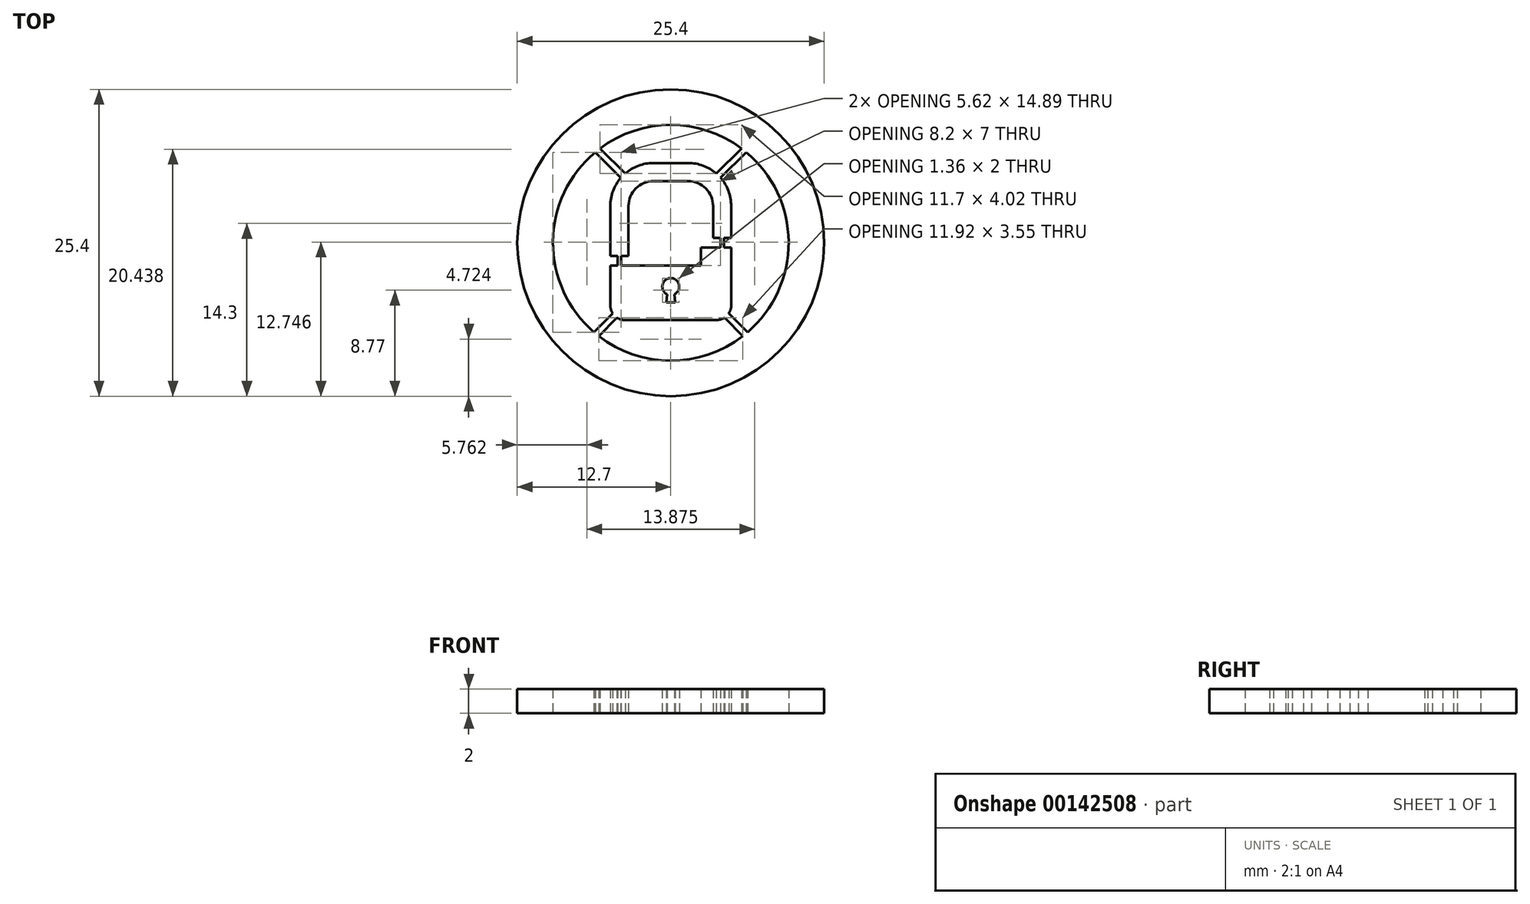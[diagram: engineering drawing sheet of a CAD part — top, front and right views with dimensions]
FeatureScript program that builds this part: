
annotation { "Feature Type Name" : "Feature", "Feature Type Description" : "" }
export const myFeature = defineFeature(function(context is Context, id is Id, definition is map)
    precondition{}
    {
        {
            assignVariable(context, id + "F0", {"name" : "thick", "anyValue" : 2});
        }
        {
            var Q0;
            Q0=qCreatedBy(makeId("Top.planeOp"),FACE);
            var sketch = newSketch(context, id + "F1", { "sketchPlane" : qUnion([Q0])});
            skCircle(sketch, "E0", {"center": v(0, 0) * mm, "radius": 9.75 * mm});
            skCircle(sketch, "E1", {"center": v(0, 0) * mm, "radius": 12.7 * mm});
            skSolve(sketch);
        }
        {
            var Q0;
            Q0=qCreatedBy(makeId("Top.planeOp"),FACE);
            var sketch = newSketch(context, id + "F2", { "sketchPlane" : qUnion([Q0])});
            skLineSegment(sketch, "E2", {"start": v(-3.78, -6.4) * mm, "end": v(3.78, -6.4) * mm});
            skLineSegment(sketch, "E3", {"start": v(5, -5.18) * mm, "end": v(5, -0.4) * mm});
            skLineSegment(sketch, "E4", {"start": v(-5, -5.18) * mm, "end": v(-5, -1.9) * mm});
            skLineSegment(sketch, "E5", {"start": v(-5, -1.9) * mm, "end": v(2.5, -1.9) * mm});
            skLineSegment(sketch, "E6", {"start": v(2.5, -1.9) * mm, "end": v(2.5, -0.4) * mm});
            skLineSegment(sketch, "E7", {"start": v(2.5, -0.4) * mm, "end": v(5, -0.4) * mm});
            skArc(sketch, "E8", {"start": v(3.78, -6.4) * mm, "mid": v(4.64, -6.04) * mm, "end": v(5, -5.18) * mm});
            skArc(sketch, "E9", {"start": v(-3.78, -6.4) * mm, "mid": v(-4.64, -6.04) * mm, "end": v(-5, -5.18) * mm});
            skLineSegment(sketch, "E10", {"start": v(-5, -1.1) * mm, "end": v(-3.5, -1.1) * mm});
            skLineSegment(sketch, "E11", {"start": v(-3.5, -1.1) * mm, "end": v(-3.5, 3.03) * mm});
            skLineSegment(sketch, "E12", {"start": v(-5, -1.1) * mm, "end": v(-5, 3.03) * mm});
            skLineSegment(sketch, "E13", {"start": v(3.5, 0.4) * mm, "end": v(5, 0.4) * mm});
            skLineSegment(sketch, "E14", {"start": v(5, 0.4) * mm, "end": v(5, 3.03) * mm});
            skLineSegment(sketch, "E15", {"start": v(3.5, 0.4) * mm, "end": v(3.5, 3.03) * mm});
            skLineSegment(sketch, "E16", {"start": v(-5, -1.9) * mm, "end": v(-5, -1.1) * mm, "construction": true});
            skLineSegment(sketch, "E17", {"start": v(5, -0.4) * mm, "end": v(5, 0.4) * mm, "construction": true});
            skLineSegment(sketch, "E18", {"start": v(-1.43, 5.1) * mm, "end": v(1.43, 5.1) * mm});
            skArc(sketch, "E19", {"start": v(-1.43, 5.1) * mm, "mid": v(-2.9, 4.5) * mm, "end": v(-3.5, 3.03) * mm});
            skArc(sketch, "E20", {"start": v(1.43, 5.1) * mm, "mid": v(2.9, 4.5) * mm, "end": v(3.5, 3.03) * mm});
            skLineSegment(sketch, "E21", {"start": v(-1.43, 6.6) * mm, "end": v(1.43, 6.6) * mm});
            skArc(sketch, "E22", {"start": v(1.43, 6.6) * mm, "mid": v(3.95, 5.55) * mm, "end": v(5, 3.03) * mm});
            skArc(sketch, "E23", {"start": v(-1.43, 6.6) * mm, "mid": v(-3.95, 5.55) * mm, "end": v(-5, 3.03) * mm});
            skSolve(sketch);
        }
        {
            var Q0;
            Q0=qCreatedBy(makeId("Top.planeOp"),FACE);
            var sketch = newSketch(context, id + "F3", { "sketchPlane" : qUnion([Q0])});
            skLineSegment(sketch, "E24", {"start": v(-0.38, -4.93) * mm, "end": v(0.38, -4.93) * mm});
            skLineSegment(sketch, "E25", {"start": v(0.38, -4.93) * mm, "end": v(0.3, -4.26) * mm});
            skLineSegment(sketch, "E26", {"start": v(0.3, -4.26) * mm, "end": v(-0.3, -4.26) * mm, "construction": true});
            skLineSegment(sketch, "E27", {"start": v(-0.3, -4.26) * mm, "end": v(-0.38, -4.93) * mm});
            skArc(sketch, "E28", {"start": v(0.3, -4.26) * mm, "mid": v(0, -2.93) * mm, "end": v(-0.3, -4.26) * mm});
            skSolve(sketch);
        }
        {
            var Q0;
            Q0=qCreatedBy(makeId("Top.planeOp"),FACE);
            var sketch = newSketch(context, id + "F4", { "sketchPlane" : qUnion([Q0])});
            skLineSegment(sketch, "E29", {"start": v(-4.8, -5.85) * mm, "end": v(-8.35, -9.4) * mm});
            skLineSegment(sketch, "E30", {"start": v(-8.35, -9.4) * mm, "end": v(-8, -9.75) * mm});
            skLineSegment(sketch, "E31", {"start": v(-8, -9.75) * mm, "end": v(-4.45, -6.2) * mm});
            skLineSegment(sketch, "E32", {"start": v(-4.45, -6.2) * mm, "end": v(-4.8, -5.85) * mm});
            skLineSegment(sketch, "E33", {"start": v(4.45, -6.2) * mm, "end": v(8, -9.75) * mm});
            skLineSegment(sketch, "E34", {"start": v(8, -9.75) * mm, "end": v(8.35, -9.4) * mm});
            skLineSegment(sketch, "E35", {"start": v(8.35, -9.4) * mm, "end": v(4.8, -5.85) * mm});
            skLineSegment(sketch, "E36", {"start": v(4.8, -5.85) * mm, "end": v(4.45, -6.2) * mm});
            skLineSegment(sketch, "E37", {"start": v(-8.15, 9.4) * mm, "end": v(-3.5, 4.75) * mm});
            skLineSegment(sketch, "E38", {"start": v(-3.5, 4.75) * mm, "end": v(-3.15, 5.1) * mm});
            skLineSegment(sketch, "E39", {"start": v(-3.15, 5.1) * mm, "end": v(-7.8, 9.75) * mm});
            skLineSegment(sketch, "E40", {"start": v(-7.8, 9.75) * mm, "end": v(-8.15, 9.4) * mm});
            skLineSegment(sketch, "E41", {"start": v(3.15, 5.1) * mm, "end": v(3.5, 4.75) * mm});
            skLineSegment(sketch, "E42", {"start": v(3.5, 4.75) * mm, "end": v(8.15, 9.4) * mm});
            skLineSegment(sketch, "E43", {"start": v(8.15, 9.4) * mm, "end": v(7.8, 9.75) * mm});
            skLineSegment(sketch, "E44", {"start": v(7.8, 9.75) * mm, "end": v(3.15, 5.1) * mm});
            skLineSegment(sketch, "E45", {"start": v(-7.8, 9.75) * mm, "end": v(7.8, 9.75) * mm});
            skLineSegment(sketch, "E46", {"start": v(-8, -9.75) * mm, "end": v(8, -9.75) * mm});
            skLineSegment(sketch, "E47.bottom", {"start": v(-4.4, -1.1) * mm, "end": v(-4.1, -1.1) * mm});
            skLineSegment(sketch, "E47.top", {"start": v(-4.4, -1.9) * mm, "end": v(-4.1, -1.9) * mm});
            skLineSegment(sketch, "E47.left", {"start": v(-4.4, -1.1) * mm, "end": v(-4.4, -1.9) * mm});
            skLineSegment(sketch, "E47.right", {"start": v(-4.1, -1.1) * mm, "end": v(-4.1, -1.9) * mm});
            skLineSegment(sketch, "E48.bottom", {"start": v(4.1, 0.4) * mm, "end": v(4.4, 0.4) * mm});
            skLineSegment(sketch, "E48.top", {"start": v(4.1, -0.4) * mm, "end": v(4.4, -0.4) * mm});
            skLineSegment(sketch, "E48.left", {"start": v(4.1, 0.4) * mm, "end": v(4.1, -0.4) * mm});
            skLineSegment(sketch, "E48.right", {"start": v(4.4, 0.4) * mm, "end": v(4.4, -0.4) * mm});
            skLineSegment(sketch, "E49", {"start": v(-4.25, -1.1) * mm, "end": v(-4.25, -1.9) * mm, "construction": true});
            skPoint(sketch, "E49.startSnap0", {"position": v(-4.25, -1.1) * mm});
            skLineSegment(sketch, "E50", {"start": v(4.25, 0.4) * mm, "end": v(4.25, -0.4) * mm, "construction": true});
            skSolve(sketch);
        }
        {
            var Q0;
            Q0=makeQuery(id+"F1.imprint","IMPRINT",FACE,{"disambiguationData":[TD([[makeQuery(id+"F1.imprint","IMPRINT",EDGE,{"derivedFrom":sQuery(id+"F1.wireOp",EDGE,"E0")}),-1.0]])]});
            extrude(context, id + "F5", {"entities" : qUnion([Q0]), "depth" : (getVariable(context, 'thick')) * mm});
        }
        {
            var Q0;
            Q0=makeQuery(id+"F4.imprint","IMPRINT",FACE,{"disambiguationData":[TD([[makeQuery(id+"F4.imprint","IMPRINT",EDGE,{"derivedFrom":sQuery(id+"F4.wireOp",EDGE,"E37")}),1.0]])]});
            var Q1;
            Q1=makeQuery(id+"F4.imprint","IMPRINT",FACE,{"disambiguationData":[TD([[makeQuery(id+"F4.imprint","IMPRINT",EDGE,{"derivedFrom":sQuery(id+"F4.wireOp",EDGE,"E41")}),1.0]])]});
            var Q2;
            Q2=makeQuery(id+"F4.imprint","IMPRINT",FACE,{"disambiguationData":[TD([[makeQuery(id+"F4.imprint","IMPRINT",EDGE,{"derivedFrom":sQuery(id+"F4.wireOp",EDGE,"E29")}),1.0]])]});
            var Q3;
            Q3=makeQuery(id+"F4.imprint","IMPRINT",FACE,{"disambiguationData":[TD([[makeQuery(id+"F4.imprint","IMPRINT",EDGE,{"derivedFrom":sQuery(id+"F4.wireOp",EDGE,"E33")}),1.0]])]});
            extrude(context, id + "F6", {"entities" : qUnion([Q0, Q1, Q2, Q3]), "operationType" : NewBodyOperationType.ADD, "depth" : (getVariable(context, 'thick')) * mm});
        }
        {
            var Q0;
            Q0=makeQuery(id+"F2.imprint","IMPRINT",FACE,{"disambiguationData":[TD([[makeQuery(id+"F2.imprint","IMPRINT",EDGE,{"derivedFrom":sQuery(id+"F2.wireOp",EDGE,"E10")}),1.0]])]});
            var Q1;
            Q1=makeQuery(id+"F2.imprint","IMPRINT",FACE,{"disambiguationData":[TD([[makeQuery(id+"F2.imprint","IMPRINT",EDGE,{"derivedFrom":sQuery(id+"F2.wireOp",EDGE,"E2")}),1.0]])]});
            extrude(context, id + "F7", {"entities" : qUnion([Q0, Q1]), "operationType" : NewBodyOperationType.ADD, "depth" : (getVariable(context, 'thick')) * mm});
        }
        {
            var Q0;
            Q0=makeQuery(id+"F3.imprint","IMPRINT",FACE,{"disambiguationData":[TD([[makeQuery(id+"F3.imprint","IMPRINT",EDGE,{"derivedFrom":sQuery(id+"F3.wireOp",EDGE,"E24")}),1.0]])]});
            extrude(context, id + "F8", {"entities" : qUnion([Q0]), "operationType" : NewBodyOperationType.REMOVE, "depth" : 25 * mm});
        }
        {
            var Q0;
            Q0=makeQuery(id+"F4.imprint","IMPRINT",FACE,{"disambiguationData":[TD([[makeQuery(id+"F4.imprint","IMPRINT",EDGE,{"derivedFrom":sQuery(id+"F4.wireOp",EDGE,"E47.bottom")}),-1.0]])]});
            var Q1;
            Q1=makeQuery(id+"F4.imprint","IMPRINT",FACE,{"disambiguationData":[TD([[makeQuery(id+"F4.imprint","IMPRINT",EDGE,{"derivedFrom":sQuery(id+"F4.wireOp",EDGE,"E48.bottom")}),-1.0]])]});
            extrude(context, id + "F9", {"entities" : qUnion([Q0, Q1]), "operationType" : NewBodyOperationType.ADD, "depth" : (getVariable(context, 'thick')) * mm});
        }
    });
